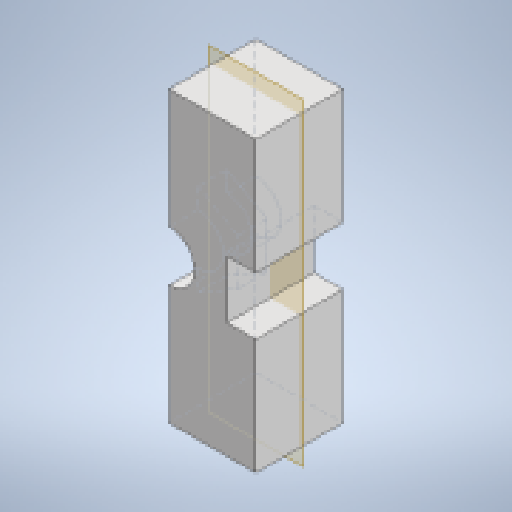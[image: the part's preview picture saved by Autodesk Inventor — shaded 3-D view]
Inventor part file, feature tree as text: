
AUTODESK INVENTOR PART (.ipt)
format: ipt  version: 2023 (Build 270158000, 158)  size: 162,304 bytes
history: native  units: mm
features: extrude x3, sketch x3, plane x1
ambient origin geometry x8: Origin, YZ Plane, XZ Plane, XY Plane, X Axis, Y Axis, Z Axis, Center Point
bodies: Solid1 (feature_tree)
feature tree (7):
  extrude  "Extrusion1"  Depth=20.0mm
  plane  "Work Plane1"
  extrude  "Extrusion2"  Depth=2.0mm
  extrude  "Extrusion3"  Depth=4.0mm
  sketch  "Sketch1"  dims[d0=20.0mm d1=20.0mm]
  sketch  "Sketch2"  dims[d2=4.0mm d6=2.0mm]
  sketch  "Sketch3"  dims[d7=2.0mm d8=4.0mm d9=2.0mm d10=5.0mm d11=0.0mm d12=5.5mm d13=1.8mm d14=0.0mm d15=3.5mm d16=8.0mm d17=0.0mm]
